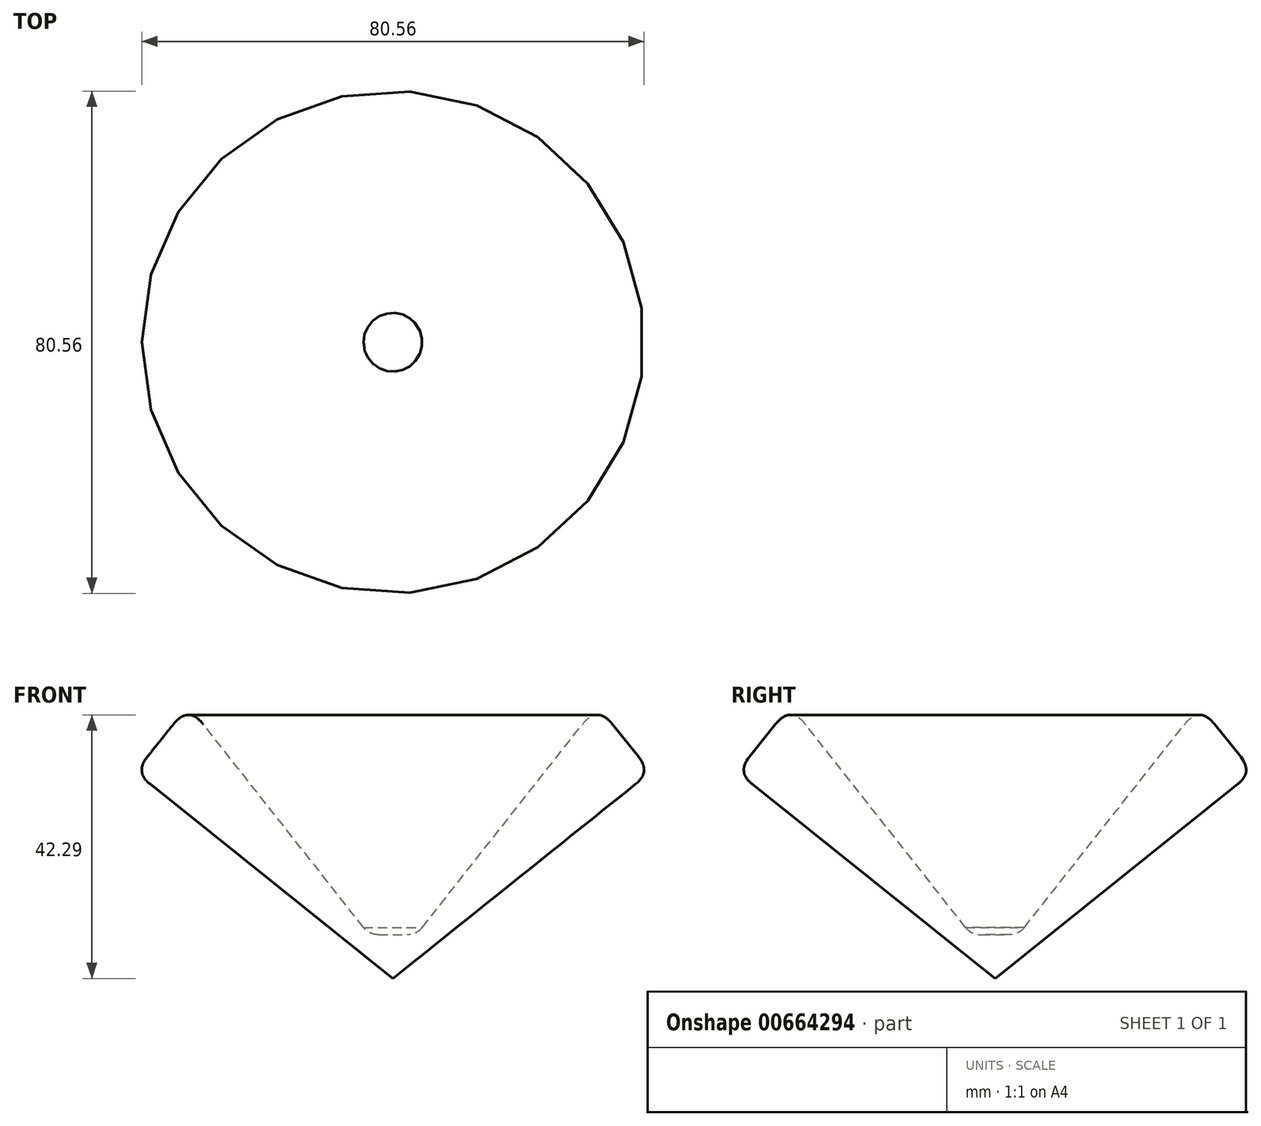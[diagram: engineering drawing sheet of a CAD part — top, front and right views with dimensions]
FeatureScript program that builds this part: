
annotation { "Feature Type Name" : "Feature", "Feature Type Description" : "" }
export const myFeature = defineFeature(function(context is Context, id is Id, definition is map)
    precondition{}
    {
        {
            var Q0;
            Q0=qCreatedBy(makeId("Front.planeOp"),FACE);
            var sketch = newSketch(context, id + "F0", { "sketchPlane" : qUnion([Q0])});
            skLineSegment(sketch, "E0", {"start": v(0, 0) * mm, "end": v(41.35, 33.11) * mm});
            skLineSegment(sketch, "E1", {"start": v(41.35, 33.11) * mm, "end": v(32.79, 43.8) * mm});
            skLineSegment(sketch, "E2", {"start": v(32.79, 43.8) * mm, "end": v(3.8, 7.03) * mm});
            skLineSegment(sketch, "E3", {"start": v(3.8, 7.03) * mm, "end": v(0, 7.03) * mm});
            skLineSegment(sketch, "E4", {"start": v(0, 7.03) * mm, "end": v(0, 0) * mm});
            skSolve(sketch);
        }
        {
            var Q0;
            Q0=makeQuery(id+"F0.imprint","IMPRINT",FACE,{"disambiguationData":[TD([[makeQuery(id+"F0.imprint","IMPRINT",EDGE,{"derivedFrom":sQuery(id+"F0.wireOp",EDGE,"E0")}),1.0]])]});
            var Q1;
            Q1=sQuery(id+"F0.wireOp",EDGE,"E4");
            revolve(context, id + "F1", {"entities" : qUnion([Q0]), "axis" : qUnion([Q1]), "revolveType" : RevolveType.FULL, "oppositeDirection" : true});
        }
        {
            var Q0;
            Q0=makeQuery(id+"F1.opRevolve","SWEPT_EDGE",EDGE,{"disambiguationData":[OSD([sQuery(id+"F0.wireOp",EDGE,"E1"),sQuery(id+"F0.wireOp",EDGE,"E2")])]});
            var Q1;
            Q1=makeQuery(id+"F1.opRevolve","SWEPT_EDGE",EDGE,{"disambiguationData":[OSD([sQuery(id+"F0.wireOp",EDGE,"E0"),sQuery(id+"F0.wireOp",EDGE,"E1")])]});
            var Q2;
            Q2=makeQuery(id+"F1.opRevolve","SWEPT_EDGE",EDGE,{"disambiguationData":[OSD([sQuery(id+"F0.wireOp",EDGE,"E2"),sQuery(id+"F0.wireOp",EDGE,"E3")])]});
            fillet(context, id + "F2", {"entities" : qUnion([Q0, Q1, Q2]), "radius" : 3.07 * mm, "tangentPropagation" : true, "rho" : 0.5, "crossSection" : FilletCrossSection.CONIC, "allowEdgeOverflow" : false});
        }
    });
